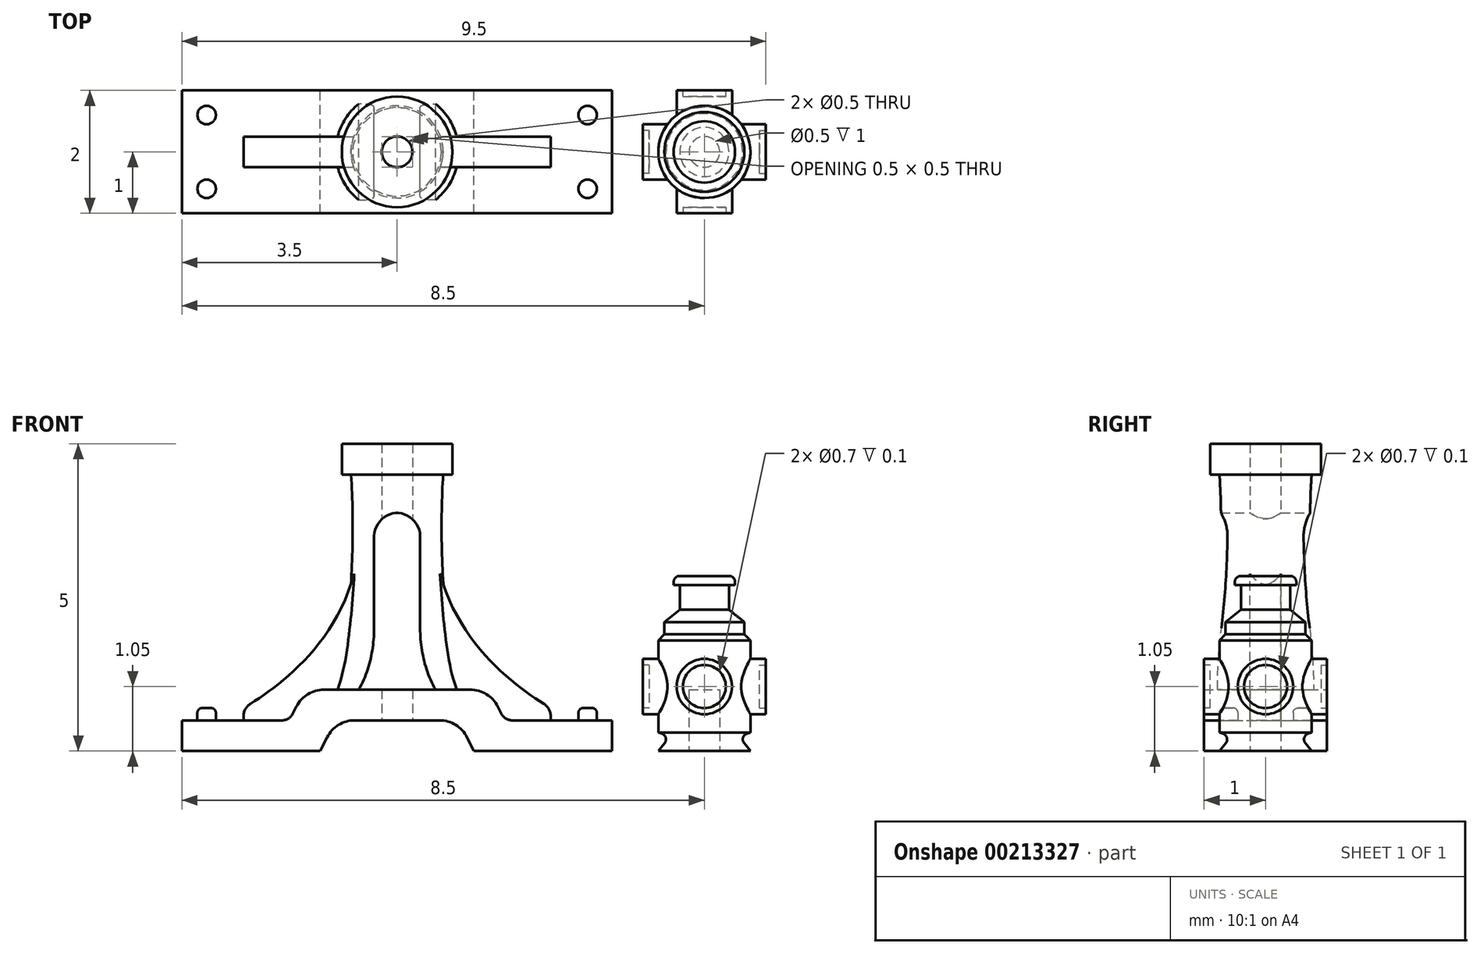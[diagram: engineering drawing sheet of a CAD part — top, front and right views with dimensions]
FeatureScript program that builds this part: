
annotation { "Feature Type Name" : "Feature", "Feature Type Description" : "" }
export const myFeature = defineFeature(function(context is Context, id is Id, definition is map)
    precondition{}
    {
        {
            var Q0;
            Q0=qCreatedBy(makeId("Top.planeOp"),FACE);
            var sketch = newSketch(context, id + "F0", { "sketchPlane" : qUnion([Q0])});
            skCircle(sketch, "E0", {"center": v(0, 0) * mm, "radius": 1 * mm});
            skSolve(sketch);
        }
        {
            var Q0;
            Q0=qCreatedBy(makeId("Top.planeOp"),FACE);
            var Q1;
            Q1 = qBodyType(qCreatedBy(id + "F7GNSJ10dKmpVkw_0" ,EDGE), BodyType.WIRE);
            cPlane(context, id + "F1", {"entities" : qUnion([Q0, Q1]), "cplaneType" : CPlaneType.OFFSET, "offset" : 4.5 * mm, "width" : 150 * mm, "height" : 150 * mm});
        }
        {
            var Q0;
            Q0=qCreatedBy(id+"F1.planeOp",FACE);
            var sketch = newSketch(context, id + "F2", { "sketchPlane" : qUnion([Q0])});
            skCircle(sketch, "E1", {"center": v(0, 0) * mm, "radius": 0.75 * mm});
            skSolve(sketch);
        }
        {
            var Q0;
            Q0=qCreatedBy(makeId("Front.planeOp"),FACE);
            var sketch = newSketch(context, id + "F3", { "sketchPlane" : qUnion([Q0])});
            skLineSegment(sketch, "E2", {"start": v(-2.5, 0) * mm, "end": v(2.5, 0) * mm});
            skLineSegment(sketch, "E3", {"start": v(0, 0) * mm, "end": v(0, 3) * mm});
            skLineSegment(sketch, "E4", {"start": v(-2.5, 0) * mm, "end": v(-2.5, 0.7) * mm});
            skFitSpline(sketch, "E5", {"points": [v(-2.5, 0.7) * mm, v(-0.67, 3) * mm], "startDerivative": vector(1.44, 0.89) * mm, "endDerivative": vector(0.94, 3.98) * mm});
            skLineSegment(sketch, "E6.MirrorCS", {"start": v(2.5, 0) * mm, "end": v(2.5, 0.7) * mm});
            skFitSpline(sketch, "E7.MirrorCS", {"points": [v(2.5, 0.7) * mm, v(0.67, 3) * mm], "startDerivative": vector(-1.44, 0.89) * mm, "endDerivative": vector(-0.94, 3.98) * mm});
            skLineSegment(sketch, "E8", {"start": v(-0.67, 3) * mm, "end": v(0.67, 3) * mm});
            skSolve(sketch);
        }
        {
            var Q0;
            Q0=makeQuery(id+"F2.imprint","IMPRINT",FACE,{"disambiguationData":[TD([[makeQuery(id+"F2.imprint","IMPRINT",EDGE,{"derivedFrom":sQuery(id+"F2.wireOp",EDGE,"E1")}),1.0]])]});
            var sketch = newSketch(context, id + "F4", { "sketchPlane" : qUnion([Q0])});
            skCircle(sketch, "E9", {"center": v(0, 0) * mm, "radius": 0.9 * mm});
            skSolve(sketch);
        }
        {
            var Q0;
            Q0=qCreatedBy(makeId("Front.planeOp"),FACE);
            var sketch = newSketch(context, id + "F5", { "sketchPlane" : qUnion([Q0])});
            skLineSegment(sketch, "E10", {"start": v(3.5, 0) * mm, "end": v(3.5, 0.5) * mm});
            skLineSegment(sketch, "E11", {"start": v(3.5, 0.5) * mm, "end": v(1.75, 0.5) * mm});
            skLineSegment(sketch, "E12", {"start": v(1.75, 0.5) * mm, "end": v(1.5, 1) * mm});
            skLineSegment(sketch, "E13", {"start": v(1.5, 1) * mm, "end": v(0, 1) * mm});
            skLineSegment(sketch, "E14", {"start": v(3.5, 0) * mm, "end": v(1.25, 0) * mm});
            skLineSegment(sketch, "E15", {"start": v(1.25, 0) * mm, "end": v(1, 0.5) * mm});
            skLineSegment(sketch, "E16", {"start": v(1, 0.5) * mm, "end": v(0, 0.5) * mm});
            skLineSegment(sketch, "E17.MirrorCS", {"start": v(-1, 0.5) * mm, "end": v(0, 0.5) * mm});
            skLineSegment(sketch, "E18.MirrorCS", {"start": v(-1.25, 0) * mm, "end": v(-1, 0.5) * mm});
            skLineSegment(sketch, "E19.MirrorCS", {"start": v(-3.5, 0) * mm, "end": v(-1.25, 0) * mm});
            skLineSegment(sketch, "E20.MirrorCS", {"start": v(-3.5, 0) * mm, "end": v(-3.5, 0.5) * mm});
            skLineSegment(sketch, "E21.MirrorCS", {"start": v(-3.5, 0.5) * mm, "end": v(-1.75, 0.5) * mm});
            skLineSegment(sketch, "E22.MirrorCS", {"start": v(-1.5, 1) * mm, "end": v(0, 1) * mm});
            skLineSegment(sketch, "E23.MirrorCS", {"start": v(-1.75, 0.5) * mm, "end": v(-1.5, 1) * mm});
            skSolve(sketch);
        }
        {
            var Q0;
            Q0=qCreatedBy(makeId("Top.planeOp"),FACE);
            cPlane(context, id + "F6", {"entities" : qUnion([Q0]), "cplaneType" : CPlaneType.OFFSET, "offset" : 1 * mm, "width" : 150 * mm, "height" : 150 * mm});
        }
        {
            var Q0;
            Q0=qCreatedBy(id+"F6.planeOp",FACE);
            var sketch = newSketch(context, id + "F7", { "sketchPlane" : qUnion([Q0])});
            skCircle(sketch, "E24", {"center": v(0, 0) * mm, "radius": 1 * mm});
            skSolve(sketch);
        }
        {
            var Q0;
            Q0=qCreatedBy(makeId("Front.planeOp"),FACE);
            var sketch = newSketch(context, id + "F8", { "sketchPlane" : qUnion([Q0])});
            skLineSegment(sketch, "E25", {"start": v(0, 4.5) * mm, "end": v(0.75, 4.5) * mm});
            skLineSegment(sketch, "E26", {"start": v(0, 4.5) * mm, "end": v(0, 1) * mm});
            skLineSegment(sketch, "E27", {"start": v(0, 1) * mm, "end": v(1, 1) * mm});
            skFitSpline(sketch, "E28", {"points": [v(0.75, 4.5) * mm, v(1, 1) * mm], "startDerivative": vector(-0.23, -3.35) * mm, "endDerivative": vector(0.7, -2.01) * mm});
            skSolve(sketch);
        }
        {
            var Q0;
            Q0 = qSketchRegion(id + "F8", true);
            var Q1;
            Q1=sQuery(id+"F8.wireOp",EDGE,"E26");
            revolve(context, id + "F9", {"entities" : qUnion([Q0]), "axis" : qUnion([Q1]), "revolveType" : RevolveType.FULL});
        }
        {
            var Q0;
            Q0 = qSketchRegion(id + "F3", true);
            extrude(context, id + "F10", {"entities" : qUnion([Q0]), "operationType" : NewBodyOperationType.ADD, "endBound" : BoundingType.SYMMETRIC, "depth" : 0.5 * mm});
        }
        {
            var Q0;
            Q0 = qSketchRegion(id + "F4", true);
            extrude(context, id + "F11", {"entities" : qUnion([Q0]), "operationType" : NewBodyOperationType.ADD, "depth" : 0.5 * mm});
        }
        {
            var Q0;
            Q0 = qSketchRegion(id + "F5", true);
            extrude(context, id + "F12", {"entities" : qUnion([Q0]), "operationType" : NewBodyOperationType.ADD, "endBound" : BoundingType.SYMMETRIC, "depth" : 2 * mm});
        }
        {
            var Q0;
            Q0=makeQuery(id+"F10.opExtrude","SWEPT_EDGE",EDGE,{"disambiguationData":[OSD([sQuery(id+"F3.wireOp",EDGE,"E6.MirrorCS"),sQuery(id+"F3.wireOp",EDGE,"E7.MirrorCS")])]});
            var Q1;
            Q1=makeQuery(id+"F10.opExtrude","SWEPT_EDGE",EDGE,{"disambiguationData":[OSD([sQuery(id+"F3.wireOp",EDGE,"E4"),sQuery(id+"F3.wireOp",EDGE,"E5")])]});
            fillet(context, id + "F13", {"entities" : qUnion([Q0, Q1]), "radius" : 0.25 * mm, "tangentPropagation" : true, "allowEdgeOverflow" : false});
        }
        {
            var Q0;
            Q0=makeQuery(id+"F12.opExtrude","SWEPT_FACE",FACE,{"disambiguationData":[OSD([sQuery(id+"F5.wireOp",EDGE,"E21.MirrorCS")])]});
            var sketch = newSketch(context, id + "F14", { "sketchPlane" : qUnion([Q0])});
            skCircle(sketch, "E29", {"center": v(-3.1, 0.6) * mm, "radius": 0.15 * mm});
            skCircle(sketch, "E30.MirrorC", {"center": v(3.1, 0.6) * mm, "radius": 0.15 * mm});
            skCircle(sketch, "E31.MirrorC", {"center": v(3.1, -0.6) * mm, "radius": 0.15 * mm});
            skCircle(sketch, "E32.MirrorC", {"center": v(-3.1, -0.6) * mm, "radius": 0.15 * mm});
            skSolve(sketch);
        }
        {
            var Q0;
            Q0 = qSketchRegion(id + "F14", true);
            extrude(context, id + "F15", {"entities" : qUnion([Q0]), "operationType" : NewBodyOperationType.ADD, "depth" : 0.2 * mm});
        }
        {
            var Q0;
            Q0=makeQuery(id+"F15.opExtrude","CAP_EDGE",EDGE,{"disambiguationData":[OSD([sQuery(id+"F14.wireOp",EDGE,"E29")])],"isStart":false});
            var Q1;
            Q1=makeQuery(id+"F15.opExtrude","CAP_EDGE",EDGE,{"disambiguationData":[OSD([sQuery(id+"F14.wireOp",EDGE,"E32.MirrorC")])],"isStart":false});
            var Q2;
            Q2=makeQuery(id+"F15.opExtrude","CAP_EDGE",EDGE,{"disambiguationData":[OSD([sQuery(id+"F14.wireOp",EDGE,"E31.MirrorC")])],"isStart":false});
            var Q3;
            Q3=makeQuery(id+"F15.opExtrude","CAP_EDGE",EDGE,{"disambiguationData":[OSD([sQuery(id+"F14.wireOp",EDGE,"E30.MirrorC")])],"isStart":false});
            fillet(context, id + "F16", {"entities" : qUnion([Q0, Q1, Q2, Q3]), "radius" : 0.07 * mm, "tangentPropagation" : true, "allowEdgeOverflow" : false});
        }
        {
            var Q0;
            Q0=qCreatedBy(makeId("Front.planeOp"),FACE);
            var sketch = newSketch(context, id + "F17", { "sketchPlane" : qUnion([Q0])});
            skLineSegment(sketch, "E33", {"start": v(-0.38, 2) * mm, "end": v(-0.38, 3.5) * mm});
            skLineSegment(sketch, "E34", {"start": v(0.37, 3.5) * mm, "end": v(0.38, 2) * mm});
            skLineSegment(sketch, "E35", {"start": v(-0.62, 1) * mm, "end": v(0.62, 1) * mm});
            skFitSpline(sketch, "E36", {"points": [v(0.38, 2) * mm, v(0.62, 1) * mm], "startDerivative": vector(0, -0.17) * mm, "endDerivative": vector(0.75, -1.32) * mm});
            skFitSpline(sketch, "E37", {"points": [v(-0.37, 2) * mm, v(-0.63, 1) * mm], "startDerivative": vector(0, -0.17) * mm, "endDerivative": vector(-0.75, -1.32) * mm});
            skArc(sketch, "E38", {"start": v(0.38, 3.5) * mm, "mid": v(0, 3.88) * mm, "end": v(-0.38, 3.5) * mm});
            skSolve(sketch);
        }
        {
            var Q0;
            Q0 = qSketchRegion(id + "F17", true);
            extrude(context, id + "F18", {"entities" : qUnion([Q0]), "operationType" : NewBodyOperationType.REMOVE, "endBound" : BoundingType.SYMMETRIC, "depth" : 25 * mm});
        }
        {
            var Q0;
            {var subQ1=sQuery(id+"F5.wireOp",EDGE,"E13");var subQ2=sQuery(id+"F5.wireOp",EDGE,"E12");Q0=makeQuery(id+"F12.boolean.opBoolean","SPLIT",EDGE,{"disambiguationData":[TD([makeQuery(id+"F10.opExtrude","CAP_FACE",FACE,{"disambiguationData":[OSD([sQuery(id+"F3.wireOp",EDGE,"E2"),sQuery(id+"F3.wireOp",EDGE,"E4"),sQuery(id+"F3.wireOp",EDGE,"E5"),sQuery(id+"F3.wireOp",EDGE,"E6.MirrorCS"),sQuery(id+"F3.wireOp",EDGE,"E7.MirrorCS"),sQuery(id+"F3.wireOp",EDGE,"E8")])],"isStart":false})])],"derivedFrom":makeQuery(id+"F12.opExtrude","SWEPT_EDGE",EDGE,{"disambiguationData":[OSD([subQ2,subQ1])]})});}
            var Q1;
            {var subQ1=sQuery(id+"F5.wireOp",EDGE,"E13");var subQ2=sQuery(id+"F5.wireOp",EDGE,"E12");Q1=makeQuery(id+"F12.boolean.opBoolean","SPLIT",EDGE,{"disambiguationData":[TD([makeQuery(id+"F10.opExtrude","CAP_FACE",FACE,{"disambiguationData":[OSD([sQuery(id+"F3.wireOp",EDGE,"E2"),sQuery(id+"F3.wireOp",EDGE,"E4"),sQuery(id+"F3.wireOp",EDGE,"E5"),sQuery(id+"F3.wireOp",EDGE,"E6.MirrorCS"),sQuery(id+"F3.wireOp",EDGE,"E7.MirrorCS"),sQuery(id+"F3.wireOp",EDGE,"E8")])],"isStart":true})])],"derivedFrom":makeQuery(id+"F12.opExtrude","SWEPT_EDGE",EDGE,{"disambiguationData":[OSD([subQ2,subQ1])]})});}
            var Q2;
            {var subQ0=sQuery(id+"F5.wireOp",EDGE,"E23.MirrorCS");var subQ1=sQuery(id+"F5.wireOp",EDGE,"E22.MirrorCS");Q2=makeQuery(id+"F12.boolean.opBoolean","SPLIT",EDGE,{"disambiguationData":[TD([makeQuery(id+"F10.opExtrude","CAP_FACE",FACE,{"disambiguationData":[OSD([sQuery(id+"F3.wireOp",EDGE,"E2"),sQuery(id+"F3.wireOp",EDGE,"E4"),sQuery(id+"F3.wireOp",EDGE,"E5"),sQuery(id+"F3.wireOp",EDGE,"E6.MirrorCS"),sQuery(id+"F3.wireOp",EDGE,"E7.MirrorCS"),sQuery(id+"F3.wireOp",EDGE,"E8")])],"isStart":false})])],"derivedFrom":makeQuery(id+"F12.opExtrude","SWEPT_EDGE",EDGE,{"disambiguationData":[OSD([subQ1,subQ0])]})});}
            var Q3;
            {var subQ0=sQuery(id+"F5.wireOp",EDGE,"E23.MirrorCS");var subQ1=sQuery(id+"F5.wireOp",EDGE,"E22.MirrorCS");Q3=makeQuery(id+"F12.boolean.opBoolean","SPLIT",EDGE,{"disambiguationData":[TD([makeQuery(id+"F10.opExtrude","CAP_FACE",FACE,{"disambiguationData":[OSD([sQuery(id+"F3.wireOp",EDGE,"E2"),sQuery(id+"F3.wireOp",EDGE,"E4"),sQuery(id+"F3.wireOp",EDGE,"E5"),sQuery(id+"F3.wireOp",EDGE,"E6.MirrorCS"),sQuery(id+"F3.wireOp",EDGE,"E7.MirrorCS"),sQuery(id+"F3.wireOp",EDGE,"E8")])],"isStart":true})])],"derivedFrom":makeQuery(id+"F12.opExtrude","SWEPT_EDGE",EDGE,{"disambiguationData":[OSD([subQ1,subQ0])]})});}
            var Q4;
            {var subQ1=sQuery(id+"F5.wireOp",EDGE,"E16");var subQ2=sQuery(id+"F5.wireOp",EDGE,"E15");Q4=makeQuery(id+"F12.boolean.opBoolean","SPLIT",EDGE,{"disambiguationData":[TD([makeQuery(id+"F10.opExtrude","CAP_FACE",FACE,{"disambiguationData":[OSD([sQuery(id+"F3.wireOp",EDGE,"E2"),sQuery(id+"F3.wireOp",EDGE,"E4"),sQuery(id+"F3.wireOp",EDGE,"E5"),sQuery(id+"F3.wireOp",EDGE,"E6.MirrorCS"),sQuery(id+"F3.wireOp",EDGE,"E7.MirrorCS"),sQuery(id+"F3.wireOp",EDGE,"E8")])],"isStart":false})])],"derivedFrom":makeQuery(id+"F12.opExtrude","SWEPT_EDGE",EDGE,{"disambiguationData":[OSD([subQ2,subQ1])]})});}
            var Q5;
            {var subQ1=sQuery(id+"F5.wireOp",EDGE,"E16");var subQ2=sQuery(id+"F5.wireOp",EDGE,"E15");Q5=makeQuery(id+"F12.boolean.opBoolean","SPLIT",EDGE,{"disambiguationData":[TD([makeQuery(id+"F10.opExtrude","CAP_FACE",FACE,{"disambiguationData":[OSD([sQuery(id+"F3.wireOp",EDGE,"E2"),sQuery(id+"F3.wireOp",EDGE,"E4"),sQuery(id+"F3.wireOp",EDGE,"E5"),sQuery(id+"F3.wireOp",EDGE,"E6.MirrorCS"),sQuery(id+"F3.wireOp",EDGE,"E7.MirrorCS"),sQuery(id+"F3.wireOp",EDGE,"E8")])],"isStart":true})])],"derivedFrom":makeQuery(id+"F12.opExtrude","SWEPT_EDGE",EDGE,{"disambiguationData":[OSD([subQ2,subQ1])]})});}
            var Q6;
            {var subQ0=sQuery(id+"F5.wireOp",EDGE,"E18.MirrorCS");var subQ1=sQuery(id+"F5.wireOp",EDGE,"E17.MirrorCS");Q6=makeQuery(id+"F12.boolean.opBoolean","SPLIT",EDGE,{"disambiguationData":[TD([makeQuery(id+"F10.opExtrude","CAP_FACE",FACE,{"disambiguationData":[OSD([sQuery(id+"F3.wireOp",EDGE,"E2"),sQuery(id+"F3.wireOp",EDGE,"E4"),sQuery(id+"F3.wireOp",EDGE,"E5"),sQuery(id+"F3.wireOp",EDGE,"E6.MirrorCS"),sQuery(id+"F3.wireOp",EDGE,"E7.MirrorCS"),sQuery(id+"F3.wireOp",EDGE,"E8")])],"isStart":false})])],"derivedFrom":makeQuery(id+"F12.opExtrude","SWEPT_EDGE",EDGE,{"disambiguationData":[OSD([subQ1,subQ0])]})});}
            var Q7;
            {var subQ0=sQuery(id+"F5.wireOp",EDGE,"E18.MirrorCS");var subQ1=sQuery(id+"F5.wireOp",EDGE,"E17.MirrorCS");Q7=makeQuery(id+"F12.boolean.opBoolean","SPLIT",EDGE,{"disambiguationData":[TD([makeQuery(id+"F10.opExtrude","CAP_FACE",FACE,{"disambiguationData":[OSD([sQuery(id+"F3.wireOp",EDGE,"E2"),sQuery(id+"F3.wireOp",EDGE,"E4"),sQuery(id+"F3.wireOp",EDGE,"E5"),sQuery(id+"F3.wireOp",EDGE,"E6.MirrorCS"),sQuery(id+"F3.wireOp",EDGE,"E7.MirrorCS"),sQuery(id+"F3.wireOp",EDGE,"E8")])],"isStart":true})])],"derivedFrom":makeQuery(id+"F12.opExtrude","SWEPT_EDGE",EDGE,{"disambiguationData":[OSD([subQ1,subQ0])]})});}
            fillet(context, id + "F19", {"entities" : qUnion([Q0, Q1, Q2, Q3, Q4, Q5, Q6, Q7]), "radius" : 0.5 * mm, "tangentPropagation" : true, "allowEdgeOverflow" : false});
        }
        {
            var Q0;
            {var subQ0=sQuery(id+"F5.wireOp",EDGE,"E12");var subQ1=sQuery(id+"F5.wireOp",EDGE,"E11");Q0=makeQuery(id+"F12.boolean.opBoolean","SPLIT",EDGE,{"disambiguationData":[TD([makeQuery(id+"F10.opExtrude","CAP_FACE",FACE,{"disambiguationData":[OSD([sQuery(id+"F3.wireOp",EDGE,"E2"),sQuery(id+"F3.wireOp",EDGE,"E4"),sQuery(id+"F3.wireOp",EDGE,"E5"),sQuery(id+"F3.wireOp",EDGE,"E6.MirrorCS"),sQuery(id+"F3.wireOp",EDGE,"E7.MirrorCS"),sQuery(id+"F3.wireOp",EDGE,"E8")])],"isStart":false})])],"derivedFrom":makeQuery(id+"F12.opExtrude","SWEPT_EDGE",EDGE,{"disambiguationData":[OSD([subQ1,subQ0])]})});}
            var Q1;
            {var subQ0=sQuery(id+"F5.wireOp",EDGE,"E12");var subQ1=sQuery(id+"F5.wireOp",EDGE,"E11");Q1=makeQuery(id+"F12.boolean.opBoolean","SPLIT",EDGE,{"disambiguationData":[TD([makeQuery(id+"F10.opExtrude","CAP_FACE",FACE,{"disambiguationData":[OSD([sQuery(id+"F3.wireOp",EDGE,"E2"),sQuery(id+"F3.wireOp",EDGE,"E4"),sQuery(id+"F3.wireOp",EDGE,"E5"),sQuery(id+"F3.wireOp",EDGE,"E6.MirrorCS"),sQuery(id+"F3.wireOp",EDGE,"E7.MirrorCS"),sQuery(id+"F3.wireOp",EDGE,"E8")])],"isStart":true})])],"derivedFrom":makeQuery(id+"F12.opExtrude","SWEPT_EDGE",EDGE,{"disambiguationData":[OSD([subQ1,subQ0])]})});}
            var Q2;
            {var subQ0=sQuery(id+"F5.wireOp",EDGE,"E23.MirrorCS");var subQ1=sQuery(id+"F5.wireOp",EDGE,"E21.MirrorCS");Q2=makeQuery(id+"F12.boolean.opBoolean","SPLIT",EDGE,{"disambiguationData":[TD([makeQuery(id+"F10.opExtrude","CAP_FACE",FACE,{"disambiguationData":[OSD([sQuery(id+"F3.wireOp",EDGE,"E2"),sQuery(id+"F3.wireOp",EDGE,"E4"),sQuery(id+"F3.wireOp",EDGE,"E5"),sQuery(id+"F3.wireOp",EDGE,"E6.MirrorCS"),sQuery(id+"F3.wireOp",EDGE,"E7.MirrorCS"),sQuery(id+"F3.wireOp",EDGE,"E8")])],"isStart":false})])],"derivedFrom":makeQuery(id+"F12.opExtrude","SWEPT_EDGE",EDGE,{"disambiguationData":[OSD([subQ1,subQ0])]})});}
            var Q3;
            {var subQ0=sQuery(id+"F5.wireOp",EDGE,"E23.MirrorCS");var subQ1=sQuery(id+"F5.wireOp",EDGE,"E21.MirrorCS");Q3=makeQuery(id+"F12.boolean.opBoolean","SPLIT",EDGE,{"disambiguationData":[TD([makeQuery(id+"F10.opExtrude","CAP_FACE",FACE,{"disambiguationData":[OSD([sQuery(id+"F3.wireOp",EDGE,"E2"),sQuery(id+"F3.wireOp",EDGE,"E4"),sQuery(id+"F3.wireOp",EDGE,"E5"),sQuery(id+"F3.wireOp",EDGE,"E6.MirrorCS"),sQuery(id+"F3.wireOp",EDGE,"E7.MirrorCS"),sQuery(id+"F3.wireOp",EDGE,"E8")])],"isStart":true})])],"derivedFrom":makeQuery(id+"F12.opExtrude","SWEPT_EDGE",EDGE,{"disambiguationData":[OSD([subQ1,subQ0])]})});}
            fillet(context, id + "F20", {"entities" : qUnion([Q0, Q1, Q2, Q3]), "radius" : 0.2 * mm, "tangentPropagation" : true, "allowEdgeOverflow" : false});
        }
        {
            var Q0;
            Q0=makeQuery(id+"F12.boolean.opBoolean","MERGE",FACE,{"derivedFrom":[makeQuery(id+"F10.opExtrude","SWEPT_FACE",FACE,{"disambiguationData":[OSD([sQuery(id+"F3.wireOp",EDGE,"E2")])]}),makeQuery(id+"F12.opExtrude","SWEPT_FACE",FACE,{"disambiguationData":[OSD([sQuery(id+"F5.wireOp",EDGE,"E14")])]}),makeQuery(id+"F12.opExtrude","SWEPT_FACE",FACE,{"disambiguationData":[OSD([sQuery(id+"F5.wireOp",EDGE,"E19.MirrorCS")])]})]});
            var sketch = newSketch(context, id + "F21", { "sketchPlane" : qUnion([Q0])});
            skLineSegment(sketch, "E39.bottom", {"start": v(-1.5, 0.48) * mm, "end": v(1.5, 0.48) * mm});
            skLineSegment(sketch, "E39.top", {"start": v(-1.5, -0.52) * mm, "end": v(1.5, -0.52) * mm});
            skLineSegment(sketch, "E39.left", {"start": v(-1.5, 0.48) * mm, "end": v(-1.5, -0.52) * mm});
            skLineSegment(sketch, "E39.right", {"start": v(1.5, 0.48) * mm, "end": v(1.5, -0.52) * mm});
            skSolve(sketch);
        }
        {
            var Q0;
            Q0 = qSketchRegion(id + "F21", true);
            extrude(context, id + "F22", {"entities" : qUnion([Q0]), "operationType" : NewBodyOperationType.ADD, "oppositeDirection" : true, "depth" : 0.75 * mm});
        }
        {
            var Q0;
            Q0=makeQuery(id+"F22.boolean.opBoolean","MERGE",FACE,{"derivedFrom":[makeQuery(id+"F12.boolean.opBoolean","MERGE",FACE,{"derivedFrom":[makeQuery(id+"F10.opExtrude","SWEPT_FACE",FACE,{"disambiguationData":[OSD([sQuery(id+"F3.wireOp",EDGE,"E2")])]}),makeQuery(id+"F12.opExtrude","SWEPT_FACE",FACE,{"disambiguationData":[OSD([sQuery(id+"F5.wireOp",EDGE,"E14")])]}),makeQuery(id+"F12.opExtrude","SWEPT_FACE",FACE,{"disambiguationData":[OSD([sQuery(id+"F5.wireOp",EDGE,"E19.MirrorCS")])]})]}),makeQuery(id+"F22.opExtrude","CAP_FACE",FACE,{"disambiguationData":[OSD([sQuery(id+"F21.wireOp",EDGE,"E39.bottom"),sQuery(id+"F21.wireOp",EDGE,"E39.top"),sQuery(id+"F21.wireOp",EDGE,"E39.left"),sQuery(id+"F21.wireOp",EDGE,"E39.right")])],"isStart":true})]});
            var sketch = newSketch(context, id + "F23", { "sketchPlane" : qUnion([Q0])});
            skCircle(sketch, "E40", {"center": v(0, 0) * mm, "radius": 0.25 * mm});
            skSolve(sketch);
        }
        {
            var Q0;
            Q0=makeQuery(id+"F22.opExtrude","SWEPT_FACE",FACE,{"disambiguationData":[OSD([sQuery(id+"F21.wireOp",EDGE,"E39.bottom")])]});
            var sketch = newSketch(context, id + "F24", { "sketchPlane" : qUnion([Q0])});
            skLineSegment(sketch, "E41.0", {"start": v(-0.7, 0.5) * mm, "end": v(0.7, 0.5) * mm});
            skArc(sketch, "E41.1", {"start": v(0.7, 0.5) * mm, "mid": v(0.95, 0.43) * mm, "end": v(1.14, 0.22) * mm});
            skLineSegment(sketch, "E41.2", {"start": v(1.25, 0) * mm, "end": v(1.14, 0.22) * mm});
            skLineSegment(sketch, "E41.3", {"start": v(-1.25, 0) * mm, "end": v(1.25, 0) * mm});
            skLineSegment(sketch, "E41.4", {"start": v(-1.25, 0) * mm, "end": v(-1.14, 0.22) * mm});
            skArc(sketch, "E41.5", {"start": v(-1.14, 0.22) * mm, "mid": v(-0.95, 0.43) * mm, "end": v(-0.7, 0.5) * mm});
            skSolve(sketch);
        }
        {
            var Q0;
            Q0 = qSketchRegion(id + "F24", true);
            extrude(context, id + "F25", {"entities" : qUnion([Q0]), "operationType" : NewBodyOperationType.REMOVE, "oppositeDirection" : true, "depth" : 25 * mm});
        }
        {
            var Q0;
            Q0 = qSketchRegion(id + "F23", true);
            extrude(context, id + "F26", {"entities" : qUnion([Q0]), "operationType" : NewBodyOperationType.REMOVE, "oppositeDirection" : true, "depth" : 25 * mm});
        }
        {
            var Q0;
            Q0=qCreatedBy(makeId("Right.planeOp"),FACE);
            cPlane(context, id + "F27", {"entities" : qUnion([Q0]), "cplaneType" : CPlaneType.OFFSET, "offset" : 5 * mm, "width" : 150 * mm, "height" : 150 * mm});
        }
        {
            var Q0;
            Q0=qCreatedBy(id+"F27.planeOp",FACE);
            var sketch = newSketch(context, id + "F28", { "sketchPlane" : qUnion([Q0])});
            skLineSegment(sketch, "E42", {"start": v(0, 0) * mm, "end": v(0.75, 0) * mm});
            skLineSegment(sketch, "E43", {"start": v(0.75, 0.3) * mm, "end": v(0.75, 1.8) * mm});
            skLineSegment(sketch, "E44", {"start": v(0.75, 1.8) * mm, "end": v(0.65, 1.9) * mm});
            skLineSegment(sketch, "E45", {"start": v(0.65, 1.9) * mm, "end": v(0.65, 2.1) * mm});
            skLineSegment(sketch, "E46", {"start": v(0.65, 2.1) * mm, "end": v(0.4, 2.3) * mm});
            skLineSegment(sketch, "E47", {"start": v(0.4, 2.3) * mm, "end": v(0.4, 2.7) * mm});
            skLineSegment(sketch, "E48", {"start": v(0.4, 2.7) * mm, "end": v(0, 2.7) * mm});
            skLineSegment(sketch, "E49", {"start": v(0, 2.7) * mm, "end": v(0, 0) * mm});
            skLineSegment(sketch, "E50", {"start": v(0.75, 0.3) * mm, "end": v(0.55, 0.25) * mm});
            skLineSegment(sketch, "E51", {"start": v(0.55, 0.25) * mm, "end": v(0.75, 0) * mm});
            skSolve(sketch);
        }
        {
            var Q0;
            Q0 = qSketchRegion(id + "F28", true);
            var Q1;
            Q1=sQuery(id+"F28.wireOp",EDGE,"E49");
            revolve(context, id + "F29", {"entities" : qUnion([Q0]), "axis" : qUnion([Q1]), "revolveType" : RevolveType.FULL});
        }
        {
            var Q0;
            Q0=makeQuery(id+"F29.opRevolve","SWEPT_FACE",FACE,{"disambiguationData":[OSD([sQuery(id+"F28.wireOp",EDGE,"E48")])]});
            var sketch = newSketch(context, id + "F30", { "sketchPlane" : qUnion([Q0])});
            skCircle(sketch, "E52", {"center": v(5, 0) * mm, "radius": 0.5 * mm});
            skSolve(sketch);
        }
        {
            var Q0;
            Q0 = qSketchRegion(id + "F30", true);
            extrude(context, id + "F31", {"entities" : qUnion([Q0]), "operationType" : NewBodyOperationType.ADD, "depth" : 0.15 * mm});
        }
        {
            var Q0;
            Q0=makeQuery(id+"F31.opExtrude","CAP_EDGE",EDGE,{"disambiguationData":[OSD([sQuery(id+"F30.wireOp",EDGE,"E52")])],"isStart":false});
            fillet(context, id + "F32", {"entities" : qUnion([Q0]), "radius" : 0.1 * mm, "tangentPropagation" : true, "allowEdgeOverflow" : false});
        }
        {
            var Q0;
            Q0=makeQuery(id+"F29.opRevolve","SWEPT_EDGE",EDGE,{"disambiguationData":[OSD([sQuery(id+"F28.wireOp",EDGE,"E50"),sQuery(id+"F28.wireOp",EDGE,"E51")])]});
            fillet(context, id + "F33", {"entities" : qUnion([Q0]), "radius" : 0.1 * mm, "tangentPropagation" : true, "allowEdgeOverflow" : false});
        }
        {
            var Q0;
            Q0=qCreatedBy(id+"F27.planeOp",FACE);
            var sketch = newSketch(context, id + "F34", { "sketchPlane" : qUnion([Q0])});
            skCircle(sketch, "E53", {"center": v(0, 1.05) * mm, "radius": 0.45 * mm});
            skSolve(sketch);
        }
        {
            var Q0;
            Q0 = qSketchRegion(id + "F34", true);
            extrude(context, id + "F35", {"entities" : qUnion([Q0]), "operationType" : NewBodyOperationType.ADD, "endBound" : BoundingType.SYMMETRIC, "depth" : 2 * mm});
        }
        {
            var Q0;
            Q0=qCreatedBy(makeId("Front.planeOp"),FACE);
            var sketch = newSketch(context, id + "F36", { "sketchPlane" : qUnion([Q0])});
            skCircle(sketch, "E54", {"center": v(5, 1.05) * mm, "radius": 0.45 * mm});
            skSolve(sketch);
        }
        {
            var Q0;
            Q0 = qSketchRegion(id + "F36", true);
            extrude(context, id + "F37", {"entities" : qUnion([Q0]), "operationType" : NewBodyOperationType.ADD, "endBound" : BoundingType.SYMMETRIC, "depth" : 2 * mm});
        }
        {
            var Q0;
            Q0=makeQuery(id+"F37.opExtrude","CAP_FACE",FACE,{"disambiguationData":[OSD([sQuery(id+"F36.wireOp",EDGE,"E54")])],"isStart":true});
            var sketch = newSketch(context, id + "F38", { "sketchPlane" : qUnion([Q0])});
            skCircle(sketch, "E55", {"center": v(-5, 1.05) * mm, "radius": 0.35 * mm});
            skSolve(sketch);
        }
        {
            var Q0;
            Q0 = qSketchRegion(id + "F38", true);
            extrude(context, id + "F39", {"entities" : qUnion([Q0]), "operationType" : NewBodyOperationType.REMOVE, "oppositeDirection" : true, "depth" : 0.1 * mm});
        }
        {
            var Q0;
            Q0=makeQuery(id+"F35.opExtrude","CAP_FACE",FACE,{"disambiguationData":[OSD([sQuery(id+"F34.wireOp",EDGE,"E53")])],"isStart":true});
            var sketch = newSketch(context, id + "F40", { "sketchPlane" : qUnion([Q0])});
            skCircle(sketch, "E56", {"center": v(0, 1.05) * mm, "radius": 0.35 * mm});
            skSolve(sketch);
        }
        {
            var Q0;
            Q0 = qSketchRegion(id + "F40", true);
            extrude(context, id + "F41", {"entities" : qUnion([Q0]), "operationType" : NewBodyOperationType.REMOVE, "oppositeDirection" : true, "depth" : 0.1 * mm});
        }
        {
            var Q0;
            Q0=makeQuery(id+"F35.opExtrude","CAP_FACE",FACE,{"disambiguationData":[OSD([sQuery(id+"F34.wireOp",EDGE,"E53")])],"isStart":false});
            var sketch = newSketch(context, id + "F42", { "sketchPlane" : qUnion([Q0])});
            skCircle(sketch, "E57", {"center": v(0, 1.05) * mm, "radius": 0.35 * mm});
            skSolve(sketch);
        }
        {
            var Q0;
            Q0 = qSketchRegion(id + "F42", true);
            extrude(context, id + "F43", {"entities" : qUnion([Q0]), "operationType" : NewBodyOperationType.REMOVE, "oppositeDirection" : true, "depth" : 0.1 * mm});
        }
        {
            var Q0;
            Q0=makeQuery(id+"F37.opExtrude","CAP_FACE",FACE,{"disambiguationData":[OSD([sQuery(id+"F36.wireOp",EDGE,"E54")])],"isStart":false});
            var sketch = newSketch(context, id + "F44", { "sketchPlane" : qUnion([Q0])});
            skCircle(sketch, "E58", {"center": v(5, 1.05) * mm, "radius": 0.35 * mm});
            skSolve(sketch);
        }
        {
            var Q0;
            Q0 = qSketchRegion(id + "F44", true);
            extrude(context, id + "F45", {"entities" : qUnion([Q0]), "operationType" : NewBodyOperationType.REMOVE, "oppositeDirection" : true, "depth" : 0.1 * mm});
        }
        {
            var Q0;
            Q0=makeQuery(id+"F29.opRevolve","SWEPT_FACE",FACE,{"disambiguationData":[OSD([sQuery(id+"F28.wireOp",EDGE,"E42")])]});
            var sketch = newSketch(context, id + "F46", { "sketchPlane" : qUnion([Q0])});
            skCircle(sketch, "E59", {"center": v(5, 0) * mm, "radius": 0.25 * mm});
            skSolve(sketch);
        }
        {
            var Q0;
            Q0 = qSketchRegion(id + "F46", true);
            extrude(context, id + "F47", {"entities" : qUnion([Q0]), "operationType" : NewBodyOperationType.REMOVE, "oppositeDirection" : true, "depth" : 1 * mm});
        }
    });
